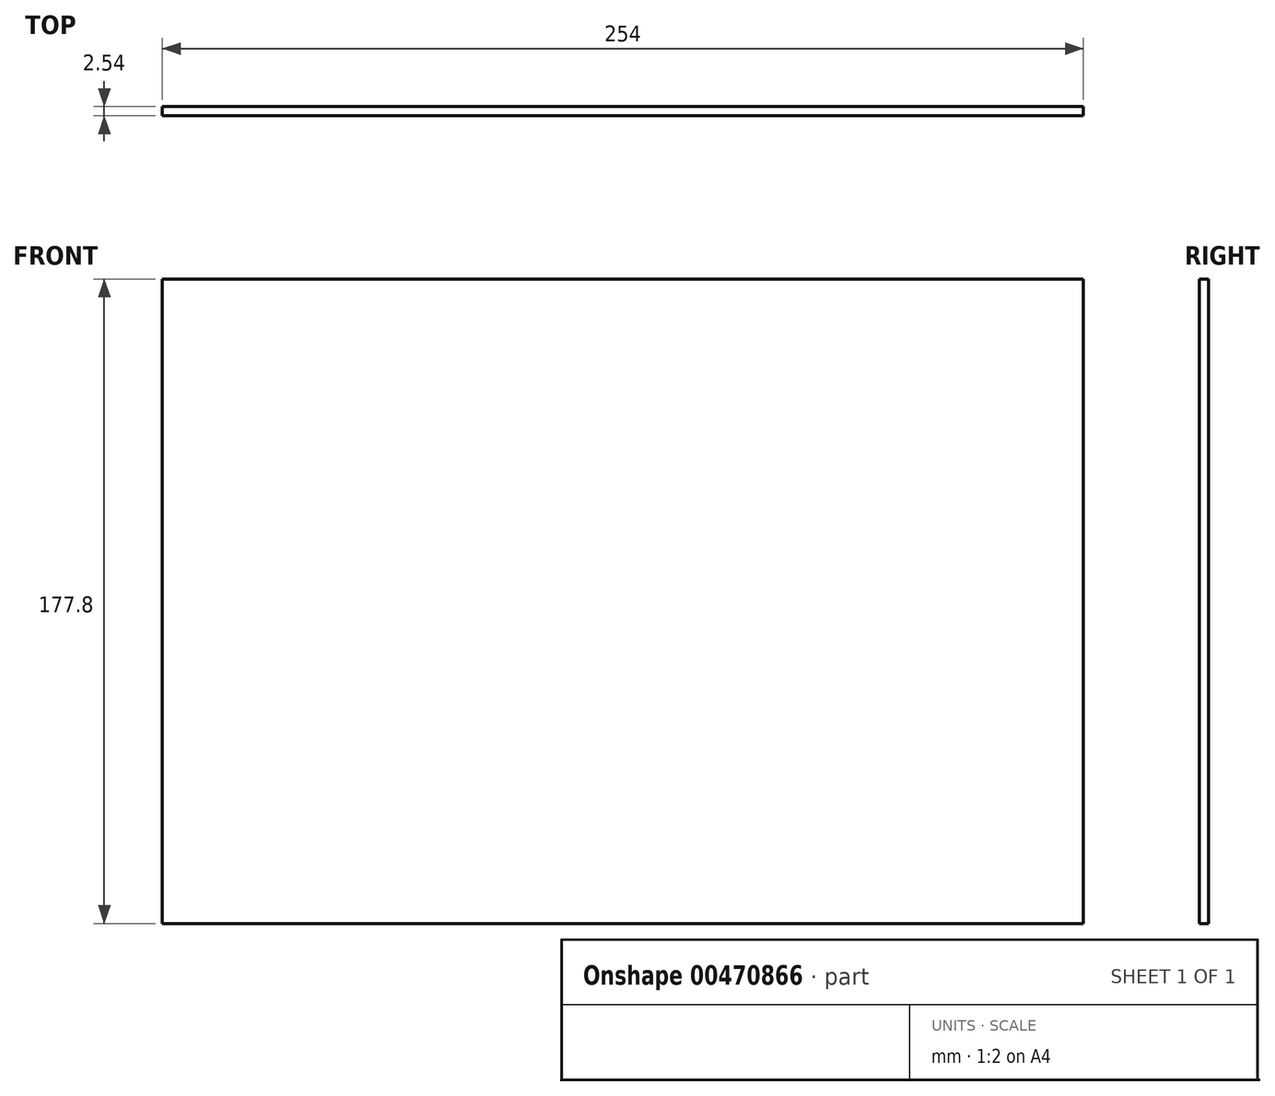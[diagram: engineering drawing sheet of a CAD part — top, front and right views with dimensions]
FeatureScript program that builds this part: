
annotation { "Feature Type Name" : "Feature", "Feature Type Description" : "" }
export const myFeature = defineFeature(function(context is Context, id is Id, definition is map)
    precondition{}
    {
        {
            var Q0;
            Q0=qCreatedBy(makeId("Front.planeOp"),FACE);
            var sketch = newSketch(context, id + "F0", { "sketchPlane" : qUnion([Q0])});
            skLineSegment(sketch, "E0.bottom", {"start": v(-121.07, 41.37) * mm, "end": v(132.93, 41.37) * mm});
            skLineSegment(sketch, "E0.top", {"start": v(-121.07, -136.43) * mm, "end": v(132.93, -136.43) * mm});
            skLineSegment(sketch, "E0.left", {"start": v(-121.07, 41.37) * mm, "end": v(-121.07, -136.43) * mm});
            skLineSegment(sketch, "E0.right", {"start": v(132.93, 41.37) * mm, "end": v(132.93, -136.43) * mm});
            skSolve(sketch);
        }
        {
            var Q0;
            Q0 = qSketchRegion(id + "FkJCh310lUfKjxP_0", true);
            var Q1;
            Q1=makeQuery(id+"F0.imprint","IMPRINT",FACE,{"disambiguationData":[TD([[makeQuery(id+"F0.imprint","IMPRINT",EDGE,{"derivedFrom":sQuery(id+"F0.wireOp",EDGE,"E0.bottom")}),-1.0]])]});
            extrude(context, id + "F1", {"entities" : qUnion([Q0, Q1]), "depth" : 2.54 * mm});
        }
    });
